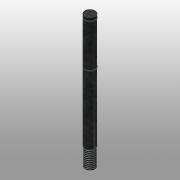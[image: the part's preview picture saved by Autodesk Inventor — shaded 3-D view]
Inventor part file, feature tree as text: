
AUTODESK INVENTOR PART (.ipt)
format: ipt  version: 2016 (Build 200138000, 138)  size: 103,936 bytes
history: native  units: mm
features: revolve x1, thread x1, sketch x1
ambient origin geometry x8: Origin, YZ Plane, XZ Plane, XY Plane, X Axis, Y Axis, Z Axis, Center Point
bodies: Solid1 (feature_tree)
feature tree (3):
  revolve  "Revolution1"  [1 undecoded]
  thread  "Thread1"  [1 undecoded]
  sketch  "Sketch1"  dims[d0=5.7mm d1=21.4mm d2=0.8mm d3=0.4mm d4=1.2mm d5=1.6mm d6=0.4mm d7=1.5mm d8=90.0deg d9=10.0mm d10=0.0mm]
note: 2 required parameter values undecoded (feature->parameter linkage not recoverable at this tier; creation-order binding heuristic only, values carry confidence <= 0.55)